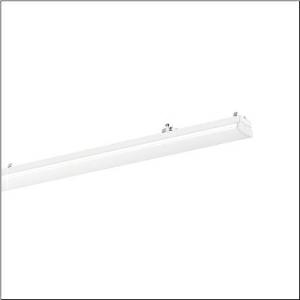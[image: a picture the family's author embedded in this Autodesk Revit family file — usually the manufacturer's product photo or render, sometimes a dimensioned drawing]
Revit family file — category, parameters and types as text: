
# Revit family: licross_11_recessed_opal_mo_51te1dmn495g
name_source: partatom
category: Lighting Fixtures
units: mm (PartAtom-declared; Revit-internal decimal feet)

## family parameters
Cut with Voids When Loaded = No
Host = Face
Light Source = No
Part Type = Normal
Room Calculation Point = No
Round Connector Dimension = Use Diameter
Shared = No

## types (1)
- --- (1 x LED, 9750 lm, 55.2 W, 4000K)
    Apparent Load = 55 VA
    CIE Flux Codes = 44 73 91 87 100
    Color Rendering = 80
    Color Temperature = 4000K
    Default Elevation = 1800 mm
    Description = Licross 11 recessed opal MO, luminaire insert, of sheet steel, coil coated, white, length: 1.500mm, width: 76mm, height: 87mm, LED rated luminous flux: 9.750lm, light colour: 840, SDCM (Standard Deviation of Colour Matching)MacAdam ≤ 2 SDCM (initial), control gear: ON/OFF Multilumen, with plug, 3-pole, with phase selection, mains connection: 220..240V, AC, 50/60Hz, rated input power: 55W, internal wiring halogen-free, primary optical cover: cover, of PMMA, light emission: direct with ceiling illumination distribution, primary light characteristic: symmetric, protection rating (complete): IP54, insulation class (complete): insulation class I (protective earthing), certification: CE, ENEC, VDE, UKCA, protection symbol: D if used in an environment with non-conductive dust loads with corresponding accessories, impact resistance: IK06, permissible ambient temperature for indoor applications: -35..+40°C, corresponds to IFS (International Featured Standards) requirements for safety and quality in the food industry, reducing of maximum allowable ambient temperature of 5°C with ceiling mounting, The light source and the operating device comply with the requirements of the Ecodesign Regulation (EU) 2019/2020 and are replaceable in accordance with this regulation, packaging unit: 1 piece
    Height = 83 mm
    Lamp = 1 x LED
    Lamp Light Flux = 9750 lm
    Lamp Power = 55.2 W
    Lamp count = 1
    Length = 1500 mm
    Luminous efficacy = 177 lm/W
    Manufacturer = Siteco
    ModVariant = No
    Model = 51TE1DMN495G
    Mounting Place = Ceiling
    Mounting Type = Pendant
    Number of Poles = 1
    OnlyDefault = Yes
    Power Factor = 1
    Product Name = Licross 11 recessed opal MO
    Product group = luminaire insert | ceiling pendant
    ProductGroupID = 901
    Protection Class = Protection class I
    Protection Degree = IP 54
    RLX_Detail_Level = 1
    RLX_Emergency_Light_Flux = 0 lm
    RLX_Emergency_Type = 0
    RLX_Emergency_Type_DB = No
    RlxData = <blob elided: 24949 chars, md5=0c9a245f>
    Socket = socket
    Standby Power = 0 W
    System Light Flux = 9750 lm
    System Power = 55 W
    Type Comments = factory setting: luminous flux: 100 % | (A | C | E) | 126 mA
    Type Image = l_1313666.jpg
    URL = http://relux.com
    VarID = @adj_083535
    Voltage = 0 V
    Weight = 0.00 kg
    Width = 76 mm

## geometry (parser evidence)
native form markers: Blend x4, Sweep x12
no freeform markers — native parametric forms only
